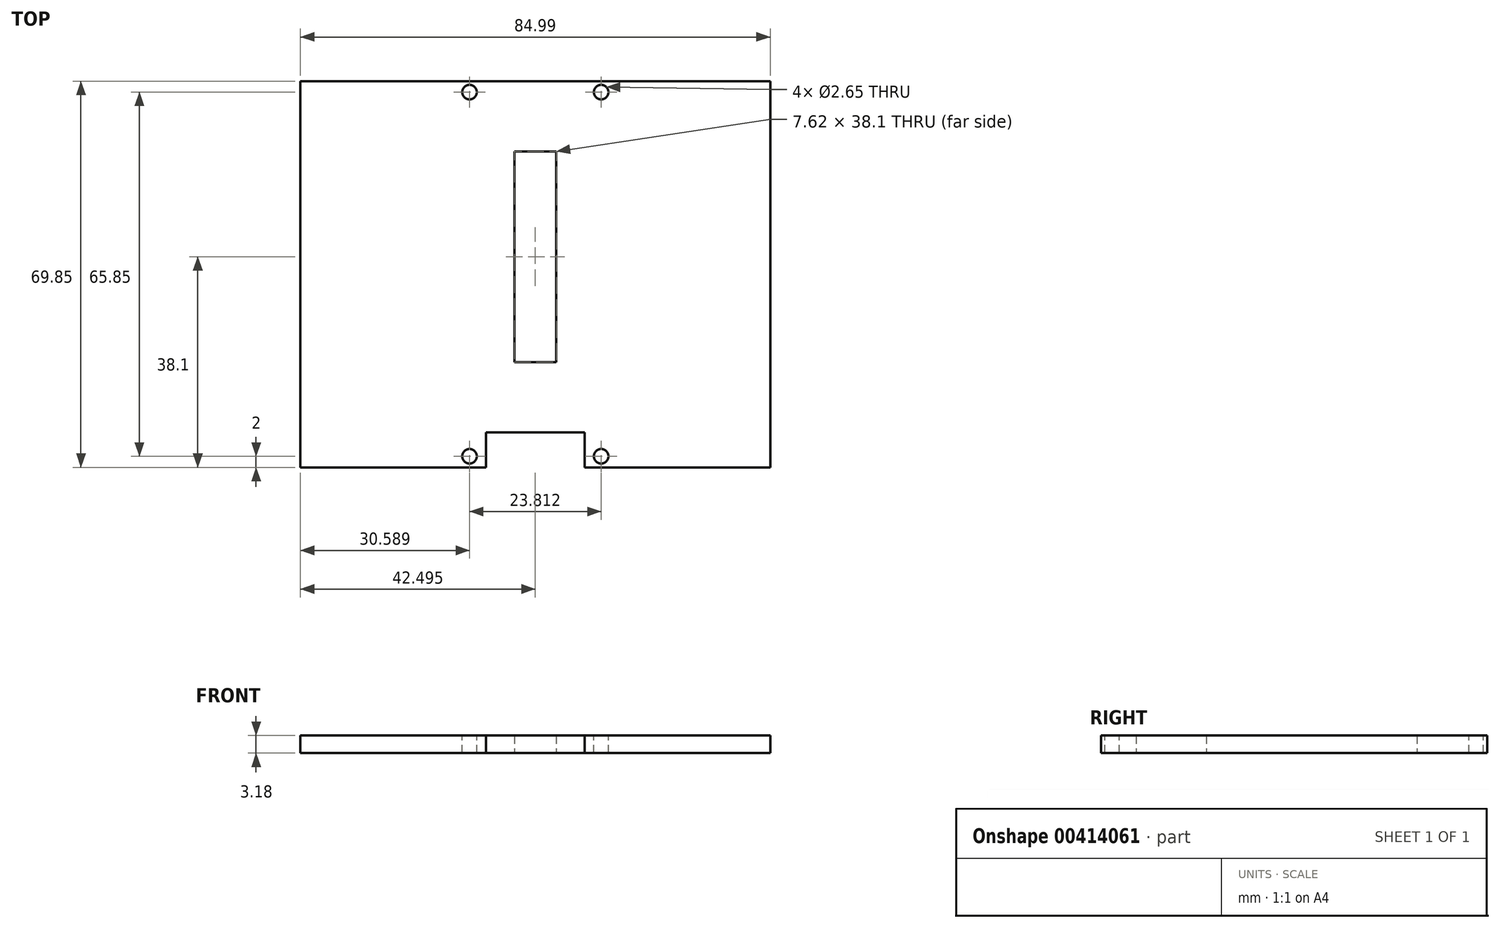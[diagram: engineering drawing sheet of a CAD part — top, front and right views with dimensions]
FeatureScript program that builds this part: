
annotation { "Feature Type Name" : "Feature", "Feature Type Description" : "" }
export const myFeature = defineFeature(function(context is Context, id is Id, definition is map)
    precondition{}
    {
        {
            var Q0;
            Q0=qCreatedBy(makeId("Top.planeOp"),FACE);
            var sketch = newSketch(context, id + "F0", { "sketchPlane" : qUnion([Q0])});
            skLineSegment(sketch, "E0.bottom", {"start": v(0, 0) * mm, "end": v(31.75, 0) * mm});
            skLineSegment(sketch, "E0.top", {"start": v(0, 63.5) * mm, "end": v(31.75, 63.5) * mm});
            skLineSegment(sketch, "E0.left", {"start": v(0, 0) * mm, "end": v(0, 63.5) * mm});
            skLineSegment(sketch, "E0.right", {"start": v(31.75, 0) * mm, "end": v(31.75, 63.5) * mm});
            skLineSegment(sketch, "E1", {"start": v(15.87, 63.5) * mm, "end": v(15.88, 0) * mm});
            skLineSegment(sketch, "E2.bottom", {"start": v(19.68, 50.8) * mm, "end": v(12.06, 50.8) * mm});
            skLineSegment(sketch, "E2.top", {"start": v(19.68, 12.7) * mm, "end": v(12.06, 12.7) * mm});
            skLineSegment(sketch, "E2.left", {"start": v(19.68, 50.8) * mm, "end": v(19.68, 12.7) * mm});
            skLineSegment(sketch, "E2.right", {"start": v(12.06, 50.8) * mm, "end": v(12.06, 12.7) * mm});
            skPoint(sketch, "E2.middle", {"position": v(15.87, 31.75) * mm});
            skSolve(sketch);
        }
        {
            var Q0;
            Q0=makeQuery(id+"F0.imprint","IMPRINT",FACE,{"disambiguationData":[TD([[makeQuery(id+"F0.imprint","IMPRINT",EDGE,{"derivedFrom":sQuery(id+"F0.wireOp",EDGE,"E0.bottom")}),1.0]])]});
            extrude(context, id + "F1", {"entities" : qUnion([Q0]), "depth" : 3.17 * mm});
        }
        {
            var Q0;
            Q0=makeQuery(id+"F1.opExtrude","SWEPT_FACE",FACE,{"disambiguationData":[OSD([sQuery(id+"F0.wireOp",EDGE,"E0.bottom")])]});
            var sketch = newSketch(context, id + "F2", { "sketchPlane" : qUnion([Q0])});
            skLineSegment(sketch, "E3", {"start": v(15.87, 3.18) * mm, "end": v(15.87, 0) * mm});
            skLineSegment(sketch, "E4.bottom", {"start": v(24.76, 3.18) * mm, "end": v(6.98, 3.18) * mm});
            skLineSegment(sketch, "E4.top", {"start": v(24.76, 0) * mm, "end": v(6.98, 0) * mm});
            skLineSegment(sketch, "E4.left", {"start": v(24.76, 3.18) * mm, "end": v(24.76, 0) * mm});
            skLineSegment(sketch, "E4.right", {"start": v(6.98, 3.18) * mm, "end": v(6.98, 0) * mm});
            skPoint(sketch, "E4.middle", {"position": v(15.87, 1.59) * mm});
            skSolve(sketch);
        }
        {
            var Q0;
            {var subQ0=sQuery(id+"F2.wireOp",EDGE,"E4.right");Q0=makeQuery(id+"F2.imprint","IMPRINT",FACE,{"disambiguationData":[TD([[makeQuery(id+"F2.imprint","IMPRINT",EDGE,{"derivedFrom":subQ0}),-1.0]])]});}
            var Q1;
            {var subQ0=sQuery(id+"F2.wireOp",EDGE,"E4.left");Q1=makeQuery(id+"F2.imprint","IMPRINT",FACE,{"disambiguationData":[TD([[makeQuery(id+"F2.imprint","IMPRINT",EDGE,{"derivedFrom":subQ0}),1.0]])]});}
            extrude(context, id + "F3", {"entities" : qUnion([Q0, Q1]), "operationType" : NewBodyOperationType.ADD, "depth" : 6.35 * mm});
        }
        {
            var Q0;
            {var subQ0=sQuery(id+"F0.wireOp",EDGE,"E0.bottom");var subQ1=makeQuery(id+"F1.opExtrude","CAP_EDGE",EDGE,{"disambiguationData":[OSD([subQ0])],"isStart":false});var subQ2=sQuery(id+"F0.wireOp",EDGE,"E0.right");var subQ4=sQuery(id+"F0.wireOp",EDGE,"E0.left");Q0=makeQuery(id+"F3.boolean.opBoolean","MERGE",FACE,{"derivedFrom":[makeQuery(id+"F1.opExtrude","CAP_FACE",FACE,{"disambiguationData":[OSD([subQ0,sQuery(id+"F0.wireOp",EDGE,"E0.top"),subQ4,subQ2])],"isStart":false}),makeQuery(id+"F3.opExtrude","SWEPT_FACE",FACE,{"disambiguationData":[OSD([subQ0]),TDD([makeQuery(id+"F2.imprint","IMPRINT",EDGE,{"disambiguationData":[TD([[makeQuery(id+"F2.imprint","INTERSECT",VERTEX,{"derivedFrom":[makeQuery(id+"F1.opExtrude","SWEPT_EDGE",EDGE,{"disambiguationData":[OSD([subQ0,subQ4])]}),subQ1]}),-1.0]])],"derivedFrom":subQ1})])]}),makeQuery(id+"F3.opExtrude","SWEPT_FACE",FACE,{"disambiguationData":[OSD([subQ0]),TDD([makeQuery(id+"F2.imprint","IMPRINT",EDGE,{"disambiguationData":[TD([[makeQuery(id+"F2.imprint","INTERSECT",VERTEX,{"derivedFrom":[makeQuery(id+"F1.opExtrude","SWEPT_EDGE",EDGE,{"disambiguationData":[OSD([subQ0,subQ2])]}),subQ1]}),1.0]])],"derivedFrom":subQ1})])]})]});}
            var sketch = newSketch(context, id + "F4", { "sketchPlane" : qUnion([Q0])});
            skLineSegment(sketch, "E5", {"start": v(3.97, -6.35) * mm, "end": v(3.97, -4.35) * mm});
            skLineSegment(sketch, "E6", {"start": v(3.97, -4.35) * mm, "end": v(27.78, -4.35) * mm});
            skLineSegment(sketch, "E7", {"start": v(27.78, -5.68) * mm, "end": v(27.78, -6.35) * mm});
            skPoint(sketch, "E8.end.orphan", {"position": v(3.5, 0) * mm});
            skPoint(sketch, "E8.start.orphan", {"position": v(3.5, -6.35) * mm});
            skPoint(sketch, "E9.end.orphan", {"position": v(28.26, 0) * mm});
            skPoint(sketch, "E9.start.orphan", {"position": v(28.26, -6.35) * mm});
            skLineSegment(sketch, "E10", {"start": v(15.87, 0) * mm, "end": v(15.87, -4.35) * mm});
            skCircle(sketch, "E11", {"center": v(3.97, -4.35) * mm, "radius": 1.32 * mm});
            skCircle(sketch, "E12", {"center": v(27.78, -4.35) * mm, "radius": 1.32 * mm});
            skLineSegment(sketch, "E13", {"start": v(27.78, -4.35) * mm, "end": v(27.78, -3.03) * mm});
            skLineSegment(sketch, "E14", {"start": v(3.97, 61.5) * mm, "end": v(27.78, 61.5) * mm});
            skCircle(sketch, "E15", {"center": v(3.97, 61.5) * mm, "radius": 1.32 * mm});
            skCircle(sketch, "E16", {"center": v(27.78, 61.5) * mm, "radius": 1.32 * mm});
            skLineSegment(sketch, "E17.trimOffspring", {"start": v(3.97, 62.82) * mm, "end": v(3.97, 63.5) * mm});
            skSolve(sketch);
        }
        {
            var Q0;
            {var subQ0=sQuery(id+"F4.wireOp",EDGE,"E6");var subQ1=sQuery(id+"F4.wireOp",EDGE,"E5");var subQ2=makeQuery(id+"F4.imprint","INTERSECT",VERTEX,{"derivedFrom":[subQ1,subQ0]});Q0=makeQuery(id+"F4.imprint","IMPRINT",FACE,{"disambiguationData":[TD([[makeQuery(id+"F4.imprint","IMPRINT",EDGE,{"disambiguationData":[TD([[subQ2,1.0]])],"derivedFrom":subQ1}),1.0]])]});}
            var Q1;
            {var subQ0=sQuery(id+"F4.wireOp",EDGE,"E6");var subQ1=sQuery(id+"F4.wireOp",EDGE,"E5");var subQ2=makeQuery(id+"F4.imprint","INTERSECT",VERTEX,{"derivedFrom":[subQ1,subQ0]});Q1=makeQuery(id+"F4.imprint","IMPRINT",FACE,{"disambiguationData":[TD([[makeQuery(id+"F4.imprint","IMPRINT",EDGE,{"disambiguationData":[TD([[subQ2,1.0]])],"derivedFrom":subQ1}),-1.0]])]});}
            var Q2;
            {var subQ0=sQuery(id+"F4.wireOp",EDGE,"E7");var subQ1=sQuery(id+"F4.wireOp",EDGE,"E6");var subQ2=makeQuery(id+"F4.imprint","INTERSECT",VERTEX,{"derivedFrom":[subQ1,subQ0]});Q2=makeQuery(id+"F4.imprint","IMPRINT",FACE,{"disambiguationData":[TD([[makeQuery(id+"F4.imprint","IMPRINT",EDGE,{"disambiguationData":[TD([[subQ2,1.0]])],"derivedFrom":subQ1}),1.0]])]});}
            var Q3;
            {var subQ0=sQuery(id+"F4.wireOp",EDGE,"E7");var subQ1=sQuery(id+"F4.wireOp",EDGE,"E6");var subQ2=makeQuery(id+"F4.imprint","INTERSECT",VERTEX,{"derivedFrom":[subQ1,subQ0]});Q3=makeQuery(id+"F4.imprint","IMPRINT",FACE,{"disambiguationData":[TD([[makeQuery(id+"F4.imprint","IMPRINT",EDGE,{"disambiguationData":[TD([[subQ2,1.0]])],"derivedFrom":subQ1}),-1.0]])]});}
            extrude(context, id + "F5", {"entities" : qUnion([Q0, Q1, Q2, Q3]), "operationType" : NewBodyOperationType.REMOVE, "oppositeDirection" : true, "depth" : 25.4 * mm});
        }
        {
            var Q0;
            {var subQ0=sQuery(id+"F4.wireOp",EDGE,"E13");Q0=makeQuery(id+"F4.imprint","IMPRINT",FACE,{"disambiguationData":[TD([[makeQuery(id+"F4.imprint","IMPRINT",EDGE,{"derivedFrom":subQ0}),-1.0]])]});}
            var Q1;
            Q1=makeQuery(id+"F4.imprint","IMPRINT",FACE,{"disambiguationData":[TD([[makeQuery(id+"F4.imprint","IMPRINT",EDGE,{"derivedFrom":sQuery(id+"F4.wireOp",EDGE,"E16")}),1.0]])]});
            var Q2;
            {var subQ0=sQuery(id+"F4.wireOp",EDGE,"E15");var subQ1=makeQuery(id+"F4.imprint","IMPRINT",VERTEX,{"disambiguationData":[OD(0.0)],"derivedFrom":subQ0});Q2=makeQuery(id+"F4.imprint","IMPRINT",FACE,{"disambiguationData":[TD([[makeQuery(id+"F4.imprint","IMPRINT",EDGE,{"disambiguationData":[TD([[subQ1,1.0]])],"derivedFrom":subQ0}),1.0]])]});}
            extrude(context, id + "F6", {"entities" : qUnion([Q0, Q1, Q2]), "operationType" : NewBodyOperationType.REMOVE, "oppositeDirection" : true, "depth" : 25.4 * mm});
        }
        {
            var Q0;
            {var subQ0=sQuery(id+"F0.wireOp",EDGE,"E0.right");Q0=makeQuery(id+"F3.boolean.opBoolean","MERGE",FACE,{"derivedFrom":[makeQuery(id+"F1.opExtrude","SWEPT_FACE",FACE,{"disambiguationData":[OSD([subQ0])]}),makeQuery(id+"F3.opExtrude","SWEPT_FACE",FACE,{"disambiguationData":[OSD([sQuery(id+"F0.wireOp",EDGE,"E0.bottom"),subQ0])]})]});}
            extrude(context, id + "F7", {"entities" : qUnion([Q0]), "operationType" : NewBodyOperationType.ADD, "depth" : 26.62 * mm, "offsetDistance" : 25.4 * mm});
        }
        {
            var Q0;
            {var subQ0=sQuery(id+"F0.wireOp",EDGE,"E0.left");Q0=makeQuery(id+"F3.boolean.opBoolean","MERGE",FACE,{"derivedFrom":[makeQuery(id+"F1.opExtrude","SWEPT_FACE",FACE,{"disambiguationData":[OSD([subQ0])]}),makeQuery(id+"F3.opExtrude","SWEPT_FACE",FACE,{"disambiguationData":[OSD([sQuery(id+"F0.wireOp",EDGE,"E0.bottom"),subQ0])]})]});}
            extrude(context, id + "F8", {"entities" : qUnion([Q0]), "operationType" : NewBodyOperationType.ADD, "depth" : 26.62 * mm, "offsetDistance" : 25.4 * mm});
        }
    });
